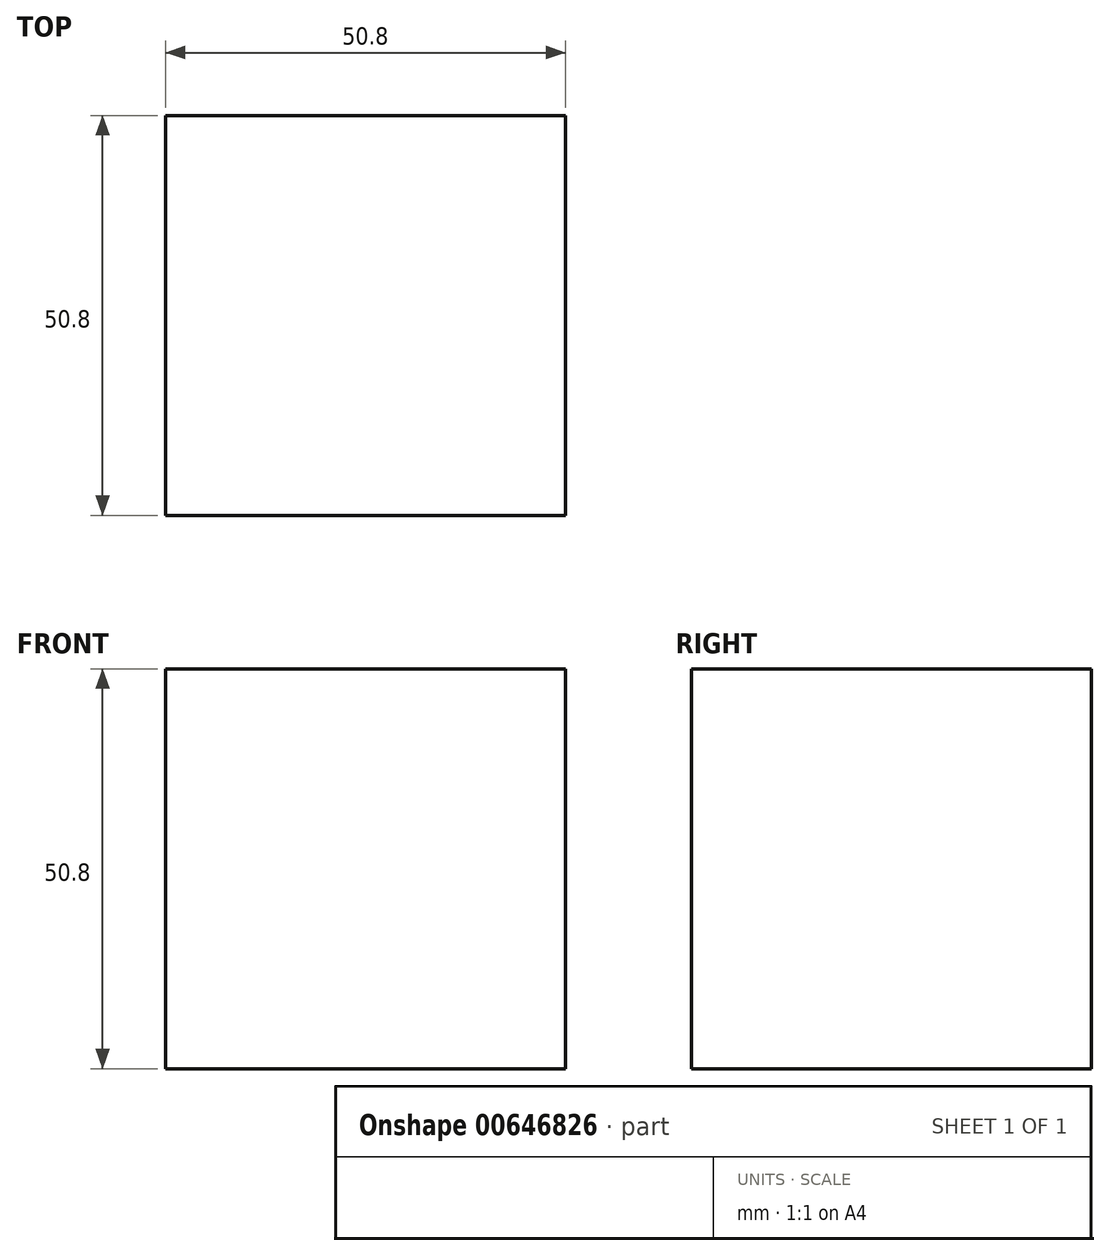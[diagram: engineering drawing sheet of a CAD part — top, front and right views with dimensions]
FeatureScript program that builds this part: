
annotation { "Feature Type Name" : "Feature", "Feature Type Description" : "" }
export const myFeature = defineFeature(function(context is Context, id is Id, definition is map)
    precondition{}
    {
        {
            var Q0;
            Q0=qCreatedBy(makeId("Top.planeOp"),FACE);
            var sketch = newSketch(context, id + "F0", { "sketchPlane" : qUnion([Q0])});
            skLineSegment(sketch, "E0.bottom", {"start": v(25.4, -25.4) * mm, "end": v(-25.4, -25.4) * mm});
            skLineSegment(sketch, "E0.top", {"start": v(25.4, 25.4) * mm, "end": v(-25.4, 25.4) * mm});
            skLineSegment(sketch, "E0.left", {"start": v(25.4, -25.4) * mm, "end": v(25.4, 25.4) * mm});
            skLineSegment(sketch, "E0.right", {"start": v(-25.4, -25.4) * mm, "end": v(-25.4, 25.4) * mm});
            skPoint(sketch, "E0.middle", {"position": v(0, 0) * mm});
            skSolve(sketch);
        }
        {
            var Q0;
            Q0=makeQuery(id+"F0.imprint","IMPRINT",FACE,{"disambiguationData":[TD([[makeQuery(id+"F0.imprint","IMPRINT",EDGE,{"derivedFrom":sQuery(id+"F0.wireOp",EDGE,"E0.bottom")}),-1.0]])]});
            var Q1;
            Q1 = qSketchRegion(id + "F0", true);
            extrude(context, id + "F1", {"entities" : qUnion([Q0, Q1]), "depth" : 50.8 * mm, "offsetDistance" : 25.4 * mm});
        }
    });
